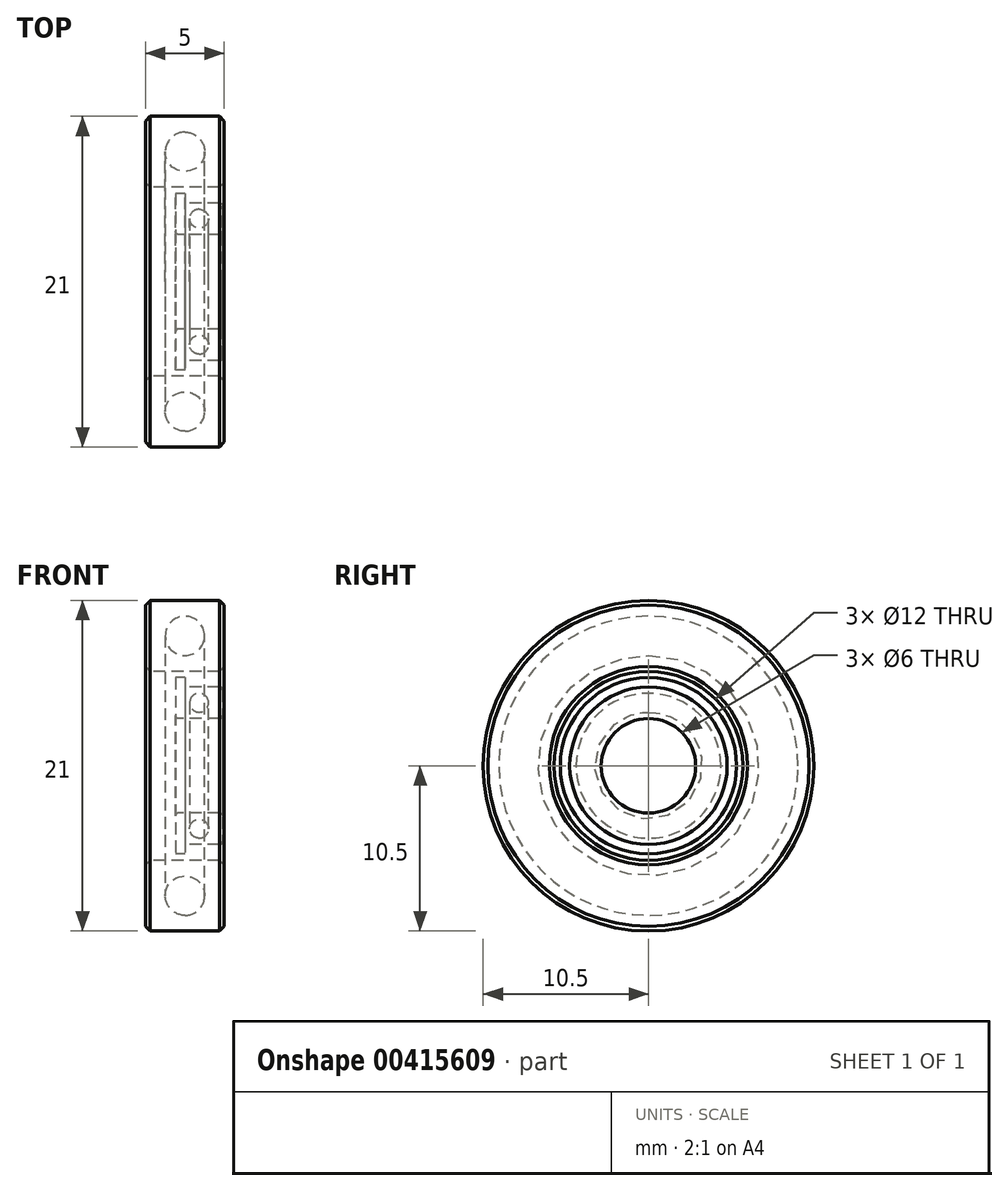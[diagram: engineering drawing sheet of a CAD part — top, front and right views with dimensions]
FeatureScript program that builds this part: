
annotation { "Feature Type Name" : "Feature", "Feature Type Description" : "" }
export const myFeature = defineFeature(function(context is Context, id is Id, definition is map)
    precondition{}
    {
        {
            var Q0;
            Q0=qCreatedBy(makeId("Front.planeOp"),FACE);
            var sketch = newSketch(context, id + "F0", { "sketchPlane" : qUnion([Q0])});
            skLineSegment(sketch, "E0", {"start": v(-0.6, 0) * mm, "end": v(2.4, 0) * mm, "construction": true});
            skLineSegment(sketch, "E1", {"start": v(-0.6, 5.6) * mm, "end": v(-0.6, 3) * mm});
            skLineSegment(sketch, "E2", {"start": v(-0.6, 3) * mm, "end": v(2.4, 3) * mm});
            skLineSegment(sketch, "E3", {"start": v(2.4, 3) * mm, "end": v(2.4, 5) * mm});
            skLineSegment(sketch, "E4", {"start": v(2.4, 5) * mm, "end": v(0, 5) * mm});
            skLineSegment(sketch, "E5", {"start": v(0, 5) * mm, "end": v(0, 5.6) * mm});
            skLineSegment(sketch, "E6", {"start": v(0, 5.6) * mm, "end": v(-0.6, 5.6) * mm});
            skCircle(sketch, "E7", {"center": v(0.9, 4) * mm, "radius": 0.6 * mm});
            skLineSegment(sketch, "E8", {"start": v(0.9, 0) * mm, "end": v(0.9, 4) * mm, "construction": true});
            skLineSegment(sketch, "E9", {"start": v(2.4, 4) * mm, "end": v(0.9, 4) * mm, "construction": true});
            skSolve(sketch);
        }
        {
            var Q0;
            Q0=makeQuery(id+"F0.imprint","IMPRINT",FACE,{"disambiguationData":[TD([[makeQuery(id+"F0.imprint","IMPRINT",EDGE,{"derivedFrom":sQuery(id+"F0.wireOp",EDGE,"E1")}),1.0]])]});
            var Q1;
            Q1=sQuery(id+"F0.wireOp",EDGE,"E0");
            revolve(context, id + "F1", {"entities" : qUnion([Q0]), "axis" : qUnion([Q1]), "revolveType" : RevolveType.FULL});
        }
        {
            var Q0;
            Q0=makeQuery(id+"F1.opRevolve","SWEPT_EDGE",EDGE,{"disambiguationData":[OSD([sQuery(id+"F0.wireOp",EDGE,"E3"),sQuery(id+"F0.wireOp",EDGE,"E4")])]});
            var Q1;
            Q1=makeQuery(id+"F1.opRevolve","SWEPT_EDGE",EDGE,{"disambiguationData":[OSD([sQuery(id+"F0.wireOp",EDGE,"E2"),sQuery(id+"F0.wireOp",EDGE,"E3")])]});
            var Q2;
            Q2=makeQuery(id+"F1.opRevolve","SWEPT_EDGE",EDGE,{"disambiguationData":[OSD([sQuery(id+"F0.wireOp",EDGE,"E1"),sQuery(id+"F0.wireOp",EDGE,"E2")])]});
            fillet(context, id + "F2", {"entities" : qUnion([Q0, Q1, Q2]), "radius" : .2 * mm, "tangentPropagation" : true, "allowEdgeOverflow" : false});
        }
        {
            var Q0;
            Q0=qCreatedBy(makeId("Front.planeOp"),FACE);
            var sketch = newSketch(context, id + "F3", { "sketchPlane" : qUnion([Q0])});
            skLineSegment(sketch, "E10", {"start": v(-2.5, 0) * mm, "end": v(2.5, 0) * mm, "construction": true});
            skLineSegment(sketch, "E11.bottom", {"start": v(-2.5, 6) * mm, "end": v(2.5, 6) * mm});
            skLineSegment(sketch, "E11.top", {"start": v(-2.5, 10.5) * mm, "end": v(2.5, 10.5) * mm});
            skLineSegment(sketch, "E11.left", {"start": v(-2.5, 6) * mm, "end": v(-2.5, 10.5) * mm});
            skLineSegment(sketch, "E11.right", {"start": v(2.5, 6) * mm, "end": v(2.5, 10.5) * mm});
            skPoint(sketch, "E11.middle", {"position": v(0, 8.25) * mm});
            skCircle(sketch, "E12", {"center": v(0, 8.25) * mm, "radius": 1.25 * mm});
            skSolve(sketch);
        }
        {
            var Q0;
            Q0=makeQuery(id+"F3.imprint","IMPRINT",FACE,{"disambiguationData":[TD([[makeQuery(id+"F3.imprint","IMPRINT",EDGE,{"derivedFrom":sQuery(id+"F3.wireOp",EDGE,"E11.bottom")}),1.0]])]});
            var Q1;
            Q1=sQuery(id+"F3.wireOp",EDGE,"E10");
            revolve(context, id + "F4", {"entities" : qUnion([Q0]), "axis" : qUnion([Q1]), "revolveType" : RevolveType.FULL});
        }
        {
            var Q0;
            Q0=makeQuery(id+"F4.opRevolve","SWEPT_FACE",FACE,{"disambiguationData":[OSD([sQuery(id+"F3.wireOp",EDGE,"E11.left")])]});
            var Q1;
            Q1=makeQuery(id+"F4.opRevolve","SWEPT_FACE",FACE,{"disambiguationData":[OSD([sQuery(id+"F3.wireOp",EDGE,"E11.right")])]});
            chamfer(context, id + "F5", {"entities" : qUnion([Q0, Q1]), "width" : .3 * mm, "tangentPropagation" : true});
        }
    });
